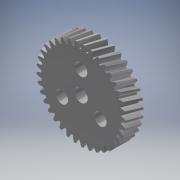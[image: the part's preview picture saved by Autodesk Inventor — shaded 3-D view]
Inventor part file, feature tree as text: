
AUTODESK INVENTOR PART (.ipt)
format: ipt  version: 2019 (Build 230136000, 136)  size: 605,696 bytes
history: native  units: mm (DEFAULTED — no unit token found)
features: sketch x4, plane x3, other x3, extrude x2, hole x1
ambient origin geometry x8: Origin, YZ Plane, XZ Plane, XY Plane, X Axis, Y Axis, Z Axis, Center Point
bodies: Solid1 (feature_tree)
feature tree (13):
  extrude  "Extrusion1"  Depth=10.0mm TaperAngle=0.0deg
  plane  "Work Plane2"
  plane  "Work Plane8"
  plane  "Work Plane9"
  other  "Spur Gear"
  extrude  "Extrusion2"  Depth=10.0mm TaperAngle=0.0deg
  hole  "Hole1"  [1 undecoded]
  sketch  "Sketch1"  dims[d0=50.240958mm d1=10.0mm d2=0.0mm]
  sketch  "Sketch2"  dims[d3=47.741935mm d4=10.0mm d5=0.0mm]
  other  "Srf1"
  sketch  "Sketch3"  dims[d16=40.0mm d17=0.0mm d34=0.849079mm]
  sketch  "Sketch4"  dims[d39=0.0mm d41=0.0mm d43=40.0mm d46=40.0mm d47=0.0mm d48=0.0mm d49=7.5mm d50=10.0mm d51=0.0mm d52=25.0mm d53=30.0mm d55=360.0deg d57=4.1mm d58=6.0mm d59=7.0mm d60=5.0mm d61=90.0deg d62=8.0mm d63=90.0deg]
  other  "Pitch Diameter"
note: 1 required parameter value undecoded (feature->parameter linkage not recoverable at this tier; creation-order binding heuristic only, values carry confidence <= 0.55)
